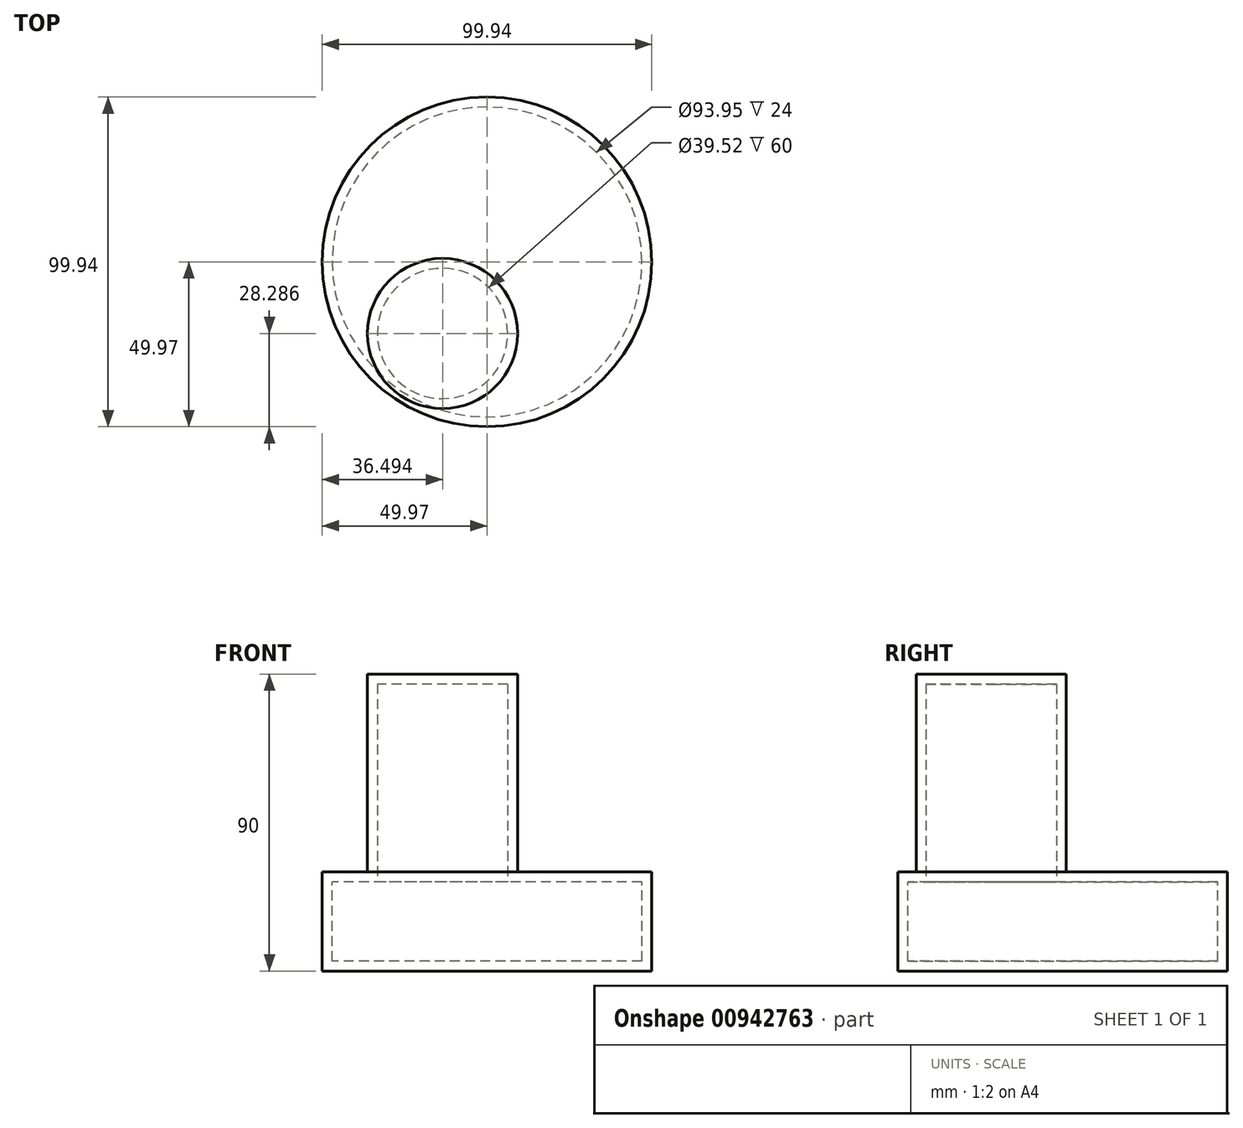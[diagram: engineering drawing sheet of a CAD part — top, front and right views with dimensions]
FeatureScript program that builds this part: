
annotation { "Feature Type Name" : "Feature", "Feature Type Description" : "" }
export const myFeature = defineFeature(function(context is Context, id is Id, definition is map)
    precondition{}
    {
        {
            var Q0;
            Q0=qCreatedBy(makeId("Top.planeOp"),FACE);
            var sketch = newSketch(context, id + "F0", { "sketchPlane" : qUnion([Q0])});
            skCircle(sketch, "E0", {"center": v(0, 0) * mm, "radius": 49.97 * mm});
            skSolve(sketch);
        }
        {
            var Q0;
            Q0=makeQuery(id+"F0.imprint","IMPRINT",FACE,{"disambiguationData":[TD([[makeQuery(id+"F0.imprint","IMPRINT",EDGE,{"derivedFrom":sQuery(id+"F0.wireOp",EDGE,"E0")}),1.0]])]});
            extrude(context, id + "F1", {"entities" : qUnion([Q0]), "oppositeDirection" : true, "depth" : 30 * mm, "offsetDistance" : 25 * mm});
        }
        {
            var Q0;
            Q0=makeQuery(id+"F1.opExtrude","CAP_FACE",FACE,{"disambiguationData":[OSD([sQuery(id+"F0.wireOp",EDGE,"E0")])],"isStart":true});
            var sketch = newSketch(context, id + "F2", { "sketchPlane" : qUnion([Q0])});
            skCircle(sketch, "E1", {"center": v(-13.48, -21.68) * mm, "radius": 22.76 * mm});
            skSolve(sketch);
        }
        {
            var Q0;
            Q0 = qSketchRegion(id + "F2", true);
            var Q1;
            Q1=makeQuery(id+"F2.imprint","IMPRINT",FACE,{"disambiguationData":[TD([[makeQuery(id+"F2.imprint","IMPRINT",EDGE,{"derivedFrom":sQuery(id+"F2.wireOp",EDGE,"E1")}),1.0]])]});
            extrude(context, id + "F3", {"entities" : qUnion([Q0, Q1]), "operationType" : NewBodyOperationType.ADD, "depth" : 60 * mm, "offsetDistance" : 25 * mm});
        }
        {
            var Q0;
            Q0=makeQuery(id+"F1.opExtrude","CAP_FACE",FACE,{"disambiguationData":[OSD([sQuery(id+"F0.wireOp",EDGE,"E0")])],"isStart":true});
            var Q1;
            Q1=makeQuery(id+"F1.opExtrude","SWEPT_FACE",FACE,{"disambiguationData":[OSD([sQuery(id+"F0.wireOp",EDGE,"E0")])]});
            var Q2;
            Q2=makeQuery(id+"F1.opExtrude","SWEPT_BODY",BODY,{"disambiguationData":[OSD([sQuery(id+"F0.wireOp",EDGE,"E0")])]});
            shell(context, id + "F4", {"isHollow" : true, "entities" : qUnion([Q0, Q1]), "parts" : qUnion([Q2]), "thickness" : 3 * mm});
        }
    });
